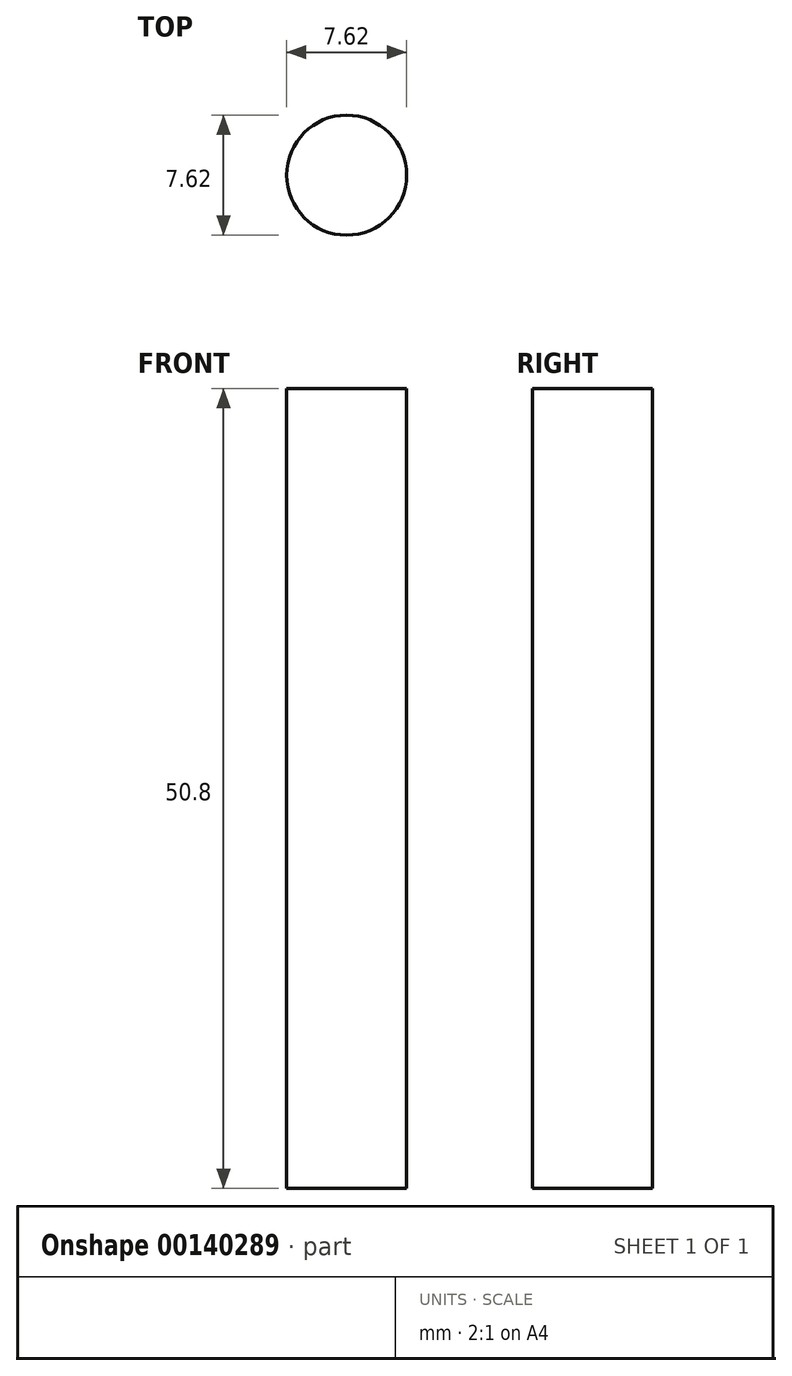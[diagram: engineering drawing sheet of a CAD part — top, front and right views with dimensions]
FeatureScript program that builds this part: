
annotation { "Feature Type Name" : "Feature", "Feature Type Description" : "" }
export const myFeature = defineFeature(function(context is Context, id is Id, definition is map)
    precondition{}
    {
        {
            var Q0;
            Q0=qCreatedBy(makeId("Top.planeOp"),FACE);
            var sketch = newSketch(context, id + "F0", { "sketchPlane" : qUnion([Q0])});
            skCircle(sketch, "E0", {"center": v(-112, 2.66) * mm, "radius": 3.81 * mm});
            skSolve(sketch);
        }
        {
            var Q0;
            Q0=makeQuery(id+"F0.imprint","IMPRINT",FACE,{"disambiguationData":[TD([[makeQuery(id+"F0.imprint","IMPRINT",EDGE,{"derivedFrom":sQuery(id+"F0.wireOp",EDGE,"E0")}),1.0]])]});
            extrude(context, id + "F1", {"entities" : qUnion([Q0]), "depth" : 50.8 * mm});
        }
    });
